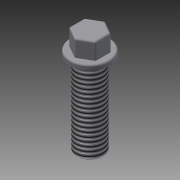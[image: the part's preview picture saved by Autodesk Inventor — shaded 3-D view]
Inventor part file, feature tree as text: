
AUTODESK INVENTOR PART (.ipt)
format: ipt  version: 2015 (Build 190159000, 159)  size: 131,584 bytes
history: native  units: mm
features: extrude x3, sketch x3, thread x1, chamfer x1, fillet x1
ambient origin geometry x8: Origin, YZ Plane, XZ Plane, XY Plane, X Axis, Y Axis, Z Axis, Center Point
bodies: 实体1 (feature_tree)
feature tree (9):
  extrude  "拉伸1"  Depth=1.5mm TaperAngle=0.0deg
  extrude  "拉伸2"  Depth=8.0mm
  extrude  "拉伸3"  Depth=8.0mm
  thread  "螺纹1"  [1 undecoded]
  chamfer  "倒角1"  Distance=10.0mm
  fillet  "圆角1"  Radius=0.5mm
  sketch  "草图1"  dims[d0=12.0mm d1=1.5mm d2=0.0mm]
  sketch  "草图2"  dims[d3=8.0mm d4=2.959103mm]
  sketch  "草图3"  dims[d5=5.0mm d6=0.0mm d7=8.0mm d8=25.0mm d9=0.0mm d10=10.0mm d11=0.0mm d12=0.5mm d13=2.0mm d14=45.0deg d15=0.5mm]
note: 1 required parameter value undecoded (feature->parameter linkage not recoverable at this tier; creation-order binding heuristic only, values carry confidence <= 0.55)
